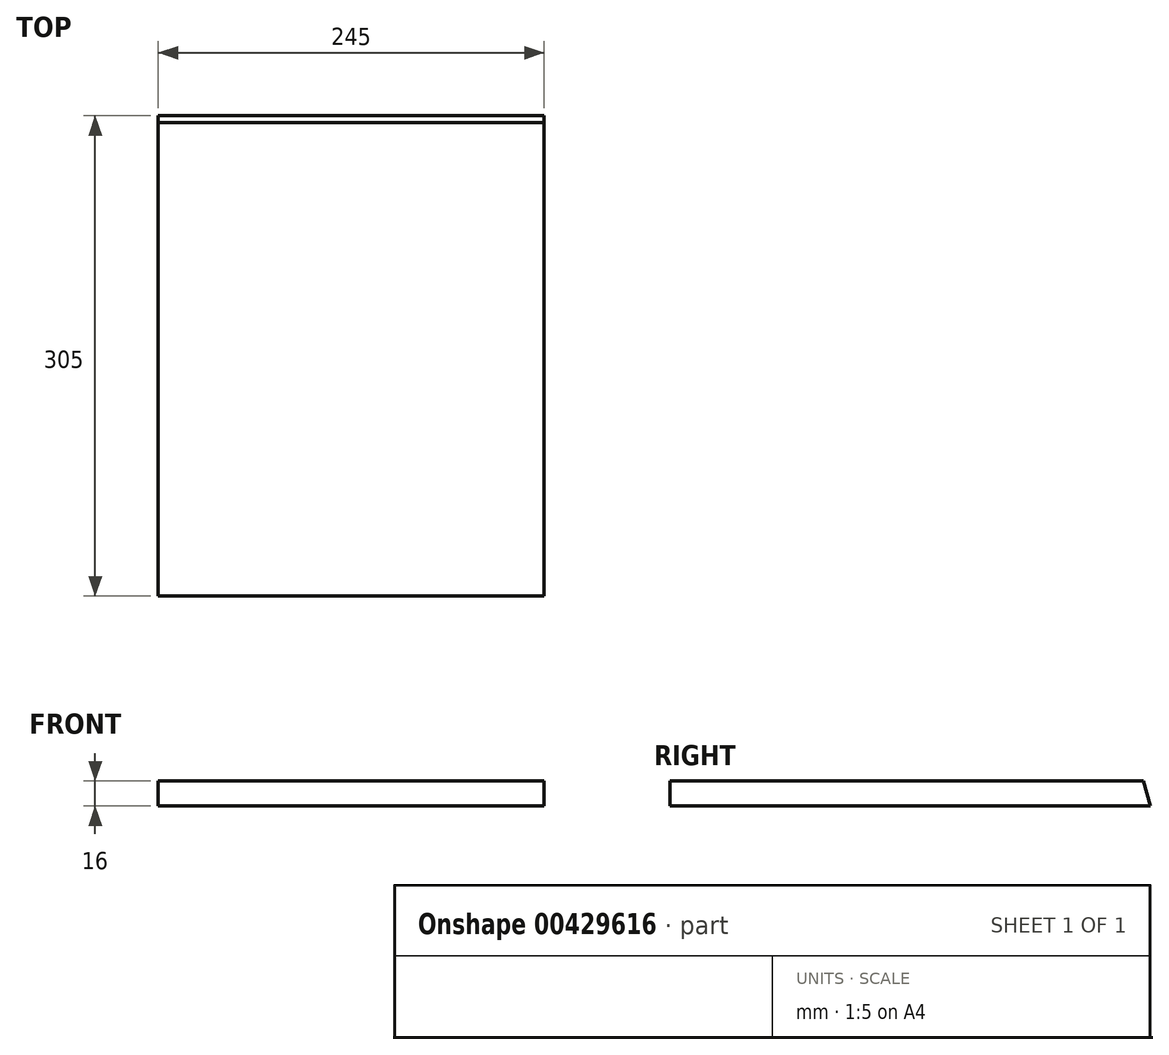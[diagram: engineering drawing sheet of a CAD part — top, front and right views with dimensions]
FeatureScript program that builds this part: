
annotation { "Feature Type Name" : "Feature", "Feature Type Description" : "" }
export const myFeature = defineFeature(function(context is Context, id is Id, definition is map)
    precondition{}
    {
        {
            var Q0;
            Q0=qCreatedBy(makeId("Top.planeOp"),FACE);
            var sketch = newSketch(context, id + "F0", { "sketchPlane" : qUnion([Q0])});
            skLineSegment(sketch, "E0.bottom", {"start": v(-122.5, 152.5) * mm, "end": v(122.5, 152.5) * mm});
            skLineSegment(sketch, "E0.top", {"start": v(-122.5, -152.5) * mm, "end": v(122.5, -152.5) * mm});
            skLineSegment(sketch, "E0.left", {"start": v(-122.5, 152.5) * mm, "end": v(-122.5, -152.5) * mm});
            skLineSegment(sketch, "E0.right", {"start": v(122.5, 152.5) * mm, "end": v(122.5, -152.5) * mm});
            skPoint(sketch, "E0.middle", {"position": v(0, 0) * mm});
            skSolve(sketch);
        }
        {
            var Q0;
            Q0 = qSketchRegion(id + "F0", true);
            extrude(context, id + "F1", {"entities" : qUnion([Q0]), "depth" : 16 * mm});
        }
        {
            var Q0;
            Q0=makeQuery(id+"F1.opExtrude","SWEPT_FACE",FACE,{"disambiguationData":[OSD([sQuery(id+"F0.wireOp",EDGE,"E0.right")])]});
            var sketch = newSketch(context, id + "F2", { "sketchPlane" : qUnion([Q0])});
            skLineSegment(sketch, "E1", {"start": v(152.5, 0) * mm, "end": v(148.21, 16) * mm});
            skLineSegment(sketch, "E2", {"start": v(148.21, 16) * mm, "end": v(152.5, 16) * mm});
            skLineSegment(sketch, "E3", {"start": v(152.5, 16) * mm, "end": v(152.5, 0) * mm});
            skSolve(sketch);
        }
        {
            var Q0;
            Q0 = qSketchRegion(id + "F2", true);
            extrude(context, id + "F3", {"entities" : qUnion([Q0]), "operationType" : NewBodyOperationType.REMOVE, "endBound" : BoundingType.THROUGH_ALL, "oppositeDirection" : true, "depth" : 25 * mm});
        }
    });
